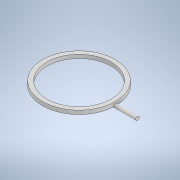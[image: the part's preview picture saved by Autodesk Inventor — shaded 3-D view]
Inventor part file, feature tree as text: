
AUTODESK INVENTOR PART (.ipt)
format: ipt  version: 2022 (Build 260153000, 153)  size: 126,976 bytes
history: native  units: in
note: dims shown in document units (in); Inventor stores cm internally (conversion verified against a paired STEP export)
features: sketch x4, extrude x3, revolve x1
ambient origin geometry x8: Origin, YZ Plane, XZ Plane, XY Plane, X Axis, Y Axis, Z Axis, Center Point
bodies: Solid1 (feature_tree)
feature tree (8):
  revolve  "Revolution1"  Angle=180.0deg
  extrude  "Extrusion1"  Depth=1.1in
  extrude  "Extrusion2"  Depth=0.125in
  extrude  "Extrusion3"  Depth=1.125in
  sketch  "Sketch1"  dims[d0=1.25in d1=180.0deg]
  sketch  "Sketch2"  dims[d2=180.0deg d4=1.1in]
  sketch  "Sketch3"  dims[d5=0.125in d6=0.0in d7=0.125in]
  sketch  "Sketch4"  dims[d8=2.0in d9=0.0in d10=0.125in d11=1.125in d12=0.0in]
